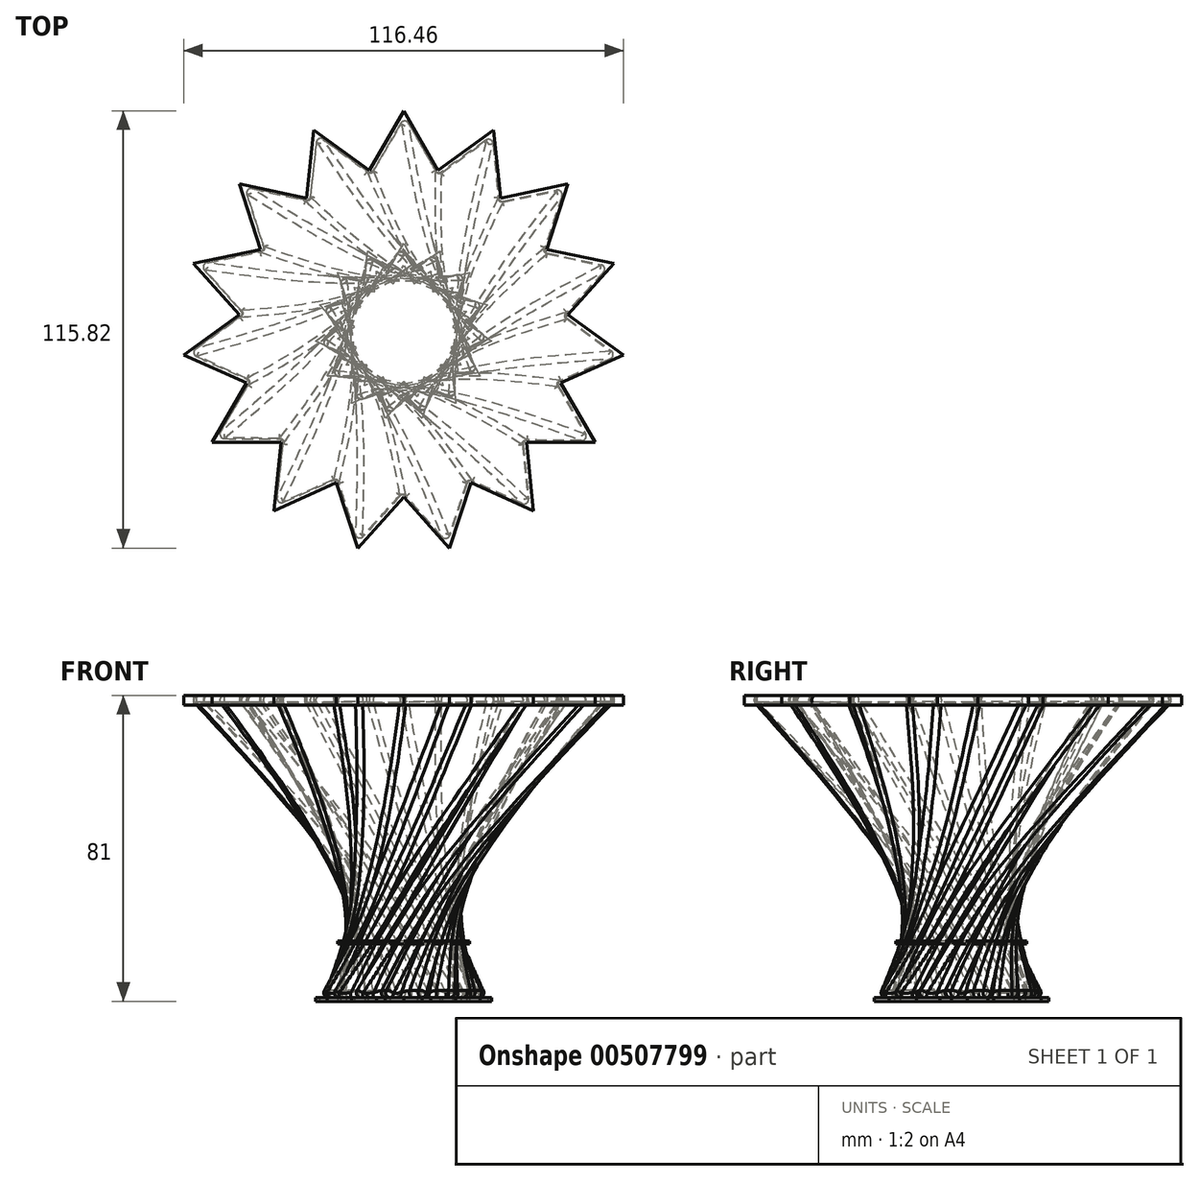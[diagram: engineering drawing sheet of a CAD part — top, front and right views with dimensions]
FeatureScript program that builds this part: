
annotation { "Feature Type Name" : "Feature", "Feature Type Description" : "" }
export const myFeature = defineFeature(function(context is Context, id is Id, definition is map)
    precondition{}
    {
        {
            assignVariable(context, id + "F0", {"name" : "BottomHeight", "anyValue" : 15});
        }
        {
            assignVariable(context, id + "F1", {"name" : "TopHeight", "anyValue" : 65});
        }
        {
            assignVariable(context, id + "F2", {"name" : "MiddleRatio", "anyValue" : 0.75});
        }
        {
            assignVariable(context, id + "F3", {"name" : "TopRatio", "anyValue" : 2.5});
        }
        {
            var Q0;
            Q0=qCreatedBy(makeId("Top.planeOp"),FACE);
            var sketch = newSketch(context, id + "F4", { "sketchPlane" : qUnion([Q0])});
            skCircle(sketch, "E0", {"center": v(0, 0) * mm, "radius": 17.5 * mm, "construction": true});
            skLineSegment(sketch, "E1", {"start": v(0, 0) * mm, "end": v(-3.64, 17.12) * mm, "construction": true});
            skLineSegment(sketch, "E2", {"start": v(-3.64, 17.12) * mm, "end": v(3.64, 17.12) * mm, "construction": true});
            skLineSegment(sketch, "E3", {"start": v(3.64, 17.12) * mm, "end": v(0, 0) * mm, "construction": true});
            skLineSegment(sketch, "E4", {"start": v(-3.64, 17.12) * mm, "end": v(0, 23.42) * mm});
            skLineSegment(sketch, "E5", {"start": v(0, 23.42) * mm, "end": v(3.64, 17.12) * mm});
            skLineSegment(sketch, "E6.1.0", {"start": v(-10.29, 14.16) * mm, "end": v(-9.53, 21.4) * mm});
            skLineSegment(sketch, "E6.1.1", {"start": v(-9.53, 21.4) * mm, "end": v(-3.64, 17.12) * mm});
            skLineSegment(sketch, "E6.2.0", {"start": v(-15.16, 8.75) * mm, "end": v(-17.4, 15.67) * mm});
            skLineSegment(sketch, "E6.2.1", {"start": v(-17.4, 15.67) * mm, "end": v(-10.29, 14.16) * mm});
            skLineSegment(sketch, "E6.3.0", {"start": v(-17.4, 1.83) * mm, "end": v(-22.27, 7.24) * mm});
            skLineSegment(sketch, "E6.3.1", {"start": v(-22.27, 7.24) * mm, "end": v(-15.16, 8.75) * mm});
            skLineSegment(sketch, "E6.4.0", {"start": v(-16.64, -5.4) * mm, "end": v(-23.3, -2.45) * mm});
            skLineSegment(sketch, "E6.4.1", {"start": v(-23.3, -2.45) * mm, "end": v(-17.4, 1.83) * mm});
            skLineSegment(sketch, "E6.5.0", {"start": v(-13, -11.7) * mm, "end": v(-20.28, -11.7) * mm});
            skLineSegment(sketch, "E6.5.1", {"start": v(-20.28, -11.7) * mm, "end": v(-16.64, -5.4) * mm});
            skLineSegment(sketch, "E6.6.0", {"start": v(-7.12, -15.99) * mm, "end": v(-13.77, -18.95) * mm});
            skLineSegment(sketch, "E6.6.1", {"start": v(-13.77, -18.95) * mm, "end": v(-13, -11.7) * mm});
            skLineSegment(sketch, "E6.7.0", {"start": v(0, -17.5) * mm, "end": v(-4.87, -22.9) * mm});
            skLineSegment(sketch, "E6.7.1", {"start": v(-4.87, -22.9) * mm, "end": v(-7.12, -15.99) * mm});
            skLineSegment(sketch, "E7.1.8.0", {"start": v(7.12, -15.99) * mm, "end": v(4.87, -22.9) * mm});
            skLineSegment(sketch, "E7.3.8.0", {"start": v(4.87, -22.9) * mm, "end": v(0, -17.5) * mm});
            skLineSegment(sketch, "E7.1.9.0", {"start": v(13, -11.7) * mm, "end": v(13.77, -18.95) * mm});
            skLineSegment(sketch, "E7.3.9.0", {"start": v(13.77, -18.95) * mm, "end": v(7.12, -15.99) * mm});
            skLineSegment(sketch, "E8.1.10.0", {"start": v(16.64, -5.4) * mm, "end": v(20.28, -11.7) * mm});
            skLineSegment(sketch, "E8.3.10.0", {"start": v(20.28, -11.7) * mm, "end": v(13, -11.7) * mm});
            skLineSegment(sketch, "E8.1.11.0", {"start": v(17.4, 1.83) * mm, "end": v(23.3, -2.45) * mm});
            skLineSegment(sketch, "E8.3.11.0", {"start": v(23.3, -2.45) * mm, "end": v(16.64, -5.4) * mm});
            skLineSegment(sketch, "E8.1.12.0", {"start": v(15.16, 8.75) * mm, "end": v(22.27, 7.24) * mm});
            skLineSegment(sketch, "E8.3.12.0", {"start": v(22.27, 7.24) * mm, "end": v(17.4, 1.83) * mm});
            skLineSegment(sketch, "E8.1.13.0", {"start": v(10.29, 14.16) * mm, "end": v(17.4, 15.67) * mm});
            skLineSegment(sketch, "E8.3.13.0", {"start": v(17.4, 15.67) * mm, "end": v(15.16, 8.75) * mm});
            skLineSegment(sketch, "E8.1.14.0", {"start": v(3.64, 17.12) * mm, "end": v(9.53, 21.4) * mm});
            skLineSegment(sketch, "E8.3.14.0", {"start": v(9.53, 21.4) * mm, "end": v(10.29, 14.16) * mm});
            skSolve(sketch);
        }
        {
            var Q0;
            Q0=makeQuery(id+"F4.imprint","IMPRINT",FACE,{"disambiguationData":[TD([[makeQuery(id+"F4.imprint","IMPRINT",EDGE,{"derivedFrom":sQuery(id+"F4.wireOp",EDGE,"E4")}),-1.0]])]});
            extrude(context, id + "F5", {"entities" : qUnion([Q0]), "depth" : 1 * mm, "offsetDistance" : 25 * mm});
        }
        {
            var Q0;
            Q0=makeQuery(id+"F5.opExtrude","SWEPT_BODY",BODY,{"disambiguationData":[OSD([sQuery(id+"F4.wireOp",EDGE,"E4"),sQuery(id+"F4.wireOp",EDGE,"E5"),sQuery(id+"F4.wireOp",EDGE,"E6.1.0"),sQuery(id+"F4.wireOp",EDGE,"E6.1.1"),sQuery(id+"F4.wireOp",EDGE,"E6.2.0"),sQuery(id+"F4.wireOp",EDGE,"E6.2.1"),sQuery(id+"F4.wireOp",EDGE,"E6.3.0"),sQuery(id+"F4.wireOp",EDGE,"E6.3.1"),sQuery(id+"F4.wireOp",EDGE,"E6.4.0"),sQuery(id+"F4.wireOp",EDGE,"E6.4.1"),sQuery(id+"F4.wireOp",EDGE,"E6.5.0"),sQuery(id+"F4.wireOp",EDGE,"E6.5.1"),sQuery(id+"F4.wireOp",EDGE,"E6.6.0"),sQuery(id+"F4.wireOp",EDGE,"E6.6.1"),sQuery(id+"F4.wireOp",EDGE,"E6.7.0"),sQuery(id+"F4.wireOp",EDGE,"E6.7.1"),sQuery(id+"F4.wireOp",EDGE,"E7.1.8.0"),sQuery(id+"F4.wireOp",EDGE,"E7.3.8.0"),sQuery(id+"F4.wireOp",EDGE,"E7.1.9.0"),sQuery(id+"F4.wireOp",EDGE,"E7.3.9.0"),sQuery(id+"F4.wireOp",EDGE,"E8.1.10.0"),sQuery(id+"F4.wireOp",EDGE,"E8.3.10.0"),sQuery(id+"F4.wireOp",EDGE,"E8.1.11.0"),sQuery(id+"F4.wireOp",EDGE,"E8.3.11.0"),sQuery(id+"F4.wireOp",EDGE,"E8.1.12.0"),sQuery(id+"F4.wireOp",EDGE,"E8.3.12.0"),sQuery(id+"F4.wireOp",EDGE,"E8.1.13.0"),sQuery(id+"F4.wireOp",EDGE,"E8.3.13.0"),sQuery(id+"F4.wireOp",EDGE,"E8.1.14.0"),sQuery(id+"F4.wireOp",EDGE,"E8.3.14.0"),sQuery(id+"F4.wireOp",EDGE,"E8.1.15.0"),sQuery(id+"F4.wireOp",EDGE,"E8.3.15.0"),sQuery(id+"F4.wireOp",EDGE,"E8.1.16.0"),sQuery(id+"F4.wireOp",EDGE,"E8.3.16.0"),sQuery(id+"F4.wireOp",EDGE,"E8.1.17.0"),sQuery(id+"F4.wireOp",EDGE,"E8.3.17.0"),sQuery(id+"F4.wireOp",EDGE,"E8.1.18.0"),sQuery(id+"F4.wireOp",EDGE,"E8.3.18.0"),sQuery(id+"F4.wireOp",EDGE,"E8.1.19.0"),sQuery(id+"F4.wireOp",EDGE,"E8.3.19.0"),sQuery(id+"F4.wireOp",EDGE,"E8.1.20.0"),sQuery(id+"F4.wireOp",EDGE,"E8.3.20.0"),sQuery(id+"F4.wireOp",EDGE,"E8.1.21.0"),sQuery(id+"F4.wireOp",EDGE,"E8.3.21.0"),sQuery(id+"F4.wireOp",EDGE,"E8.1.22.0"),sQuery(id+"F4.wireOp",EDGE,"E8.3.22.0"),sQuery(id+"F4.wireOp",EDGE,"E8.1.23.0"),sQuery(id+"F4.wireOp",EDGE,"E8.3.23.0"),sQuery(id+"F4.wireOp",EDGE,"E8.1.24.0"),sQuery(id+"F4.wireOp",EDGE,"E8.3.24.0")])]});
            transform(context, id + "F6", {"entities" : qUnion([Q0]), "transformType" : TransformType.TRANSLATION_3D, "dx" : 0 * mm, "dy" : 0 * mm, "dz" : (getVariable(context, 'BottomHeight')) * mm, "makeCopy" : true});
        }
        {
            var Q0;
            Q0=makeQuery(id+"F6.opPattern","COPY",BODY,{"derivedFrom":makeQuery(id+"F5.opExtrude","SWEPT_BODY",BODY,{"disambiguationData":[OSD([sQuery(id+"F4.wireOp",EDGE,"E4"),sQuery(id+"F4.wireOp",EDGE,"E5"),sQuery(id+"F4.wireOp",EDGE,"E6.1.0"),sQuery(id+"F4.wireOp",EDGE,"E6.1.1"),sQuery(id+"F4.wireOp",EDGE,"E6.2.0"),sQuery(id+"F4.wireOp",EDGE,"E6.2.1"),sQuery(id+"F4.wireOp",EDGE,"E6.3.0"),sQuery(id+"F4.wireOp",EDGE,"E6.3.1"),sQuery(id+"F4.wireOp",EDGE,"E6.4.0"),sQuery(id+"F4.wireOp",EDGE,"E6.4.1"),sQuery(id+"F4.wireOp",EDGE,"E6.5.0"),sQuery(id+"F4.wireOp",EDGE,"E6.5.1"),sQuery(id+"F4.wireOp",EDGE,"E6.6.0"),sQuery(id+"F4.wireOp",EDGE,"E6.6.1"),sQuery(id+"F4.wireOp",EDGE,"E6.7.0"),sQuery(id+"F4.wireOp",EDGE,"E6.7.1"),sQuery(id+"F4.wireOp",EDGE,"E7.1.8.0"),sQuery(id+"F4.wireOp",EDGE,"E7.3.8.0"),sQuery(id+"F4.wireOp",EDGE,"E7.1.9.0"),sQuery(id+"F4.wireOp",EDGE,"E7.3.9.0"),sQuery(id+"F4.wireOp",EDGE,"E8.1.10.0"),sQuery(id+"F4.wireOp",EDGE,"E8.3.10.0"),sQuery(id+"F4.wireOp",EDGE,"E8.1.11.0"),sQuery(id+"F4.wireOp",EDGE,"E8.3.11.0"),sQuery(id+"F4.wireOp",EDGE,"E8.1.12.0"),sQuery(id+"F4.wireOp",EDGE,"E8.3.12.0"),sQuery(id+"F4.wireOp",EDGE,"E8.1.13.0"),sQuery(id+"F4.wireOp",EDGE,"E8.3.13.0"),sQuery(id+"F4.wireOp",EDGE,"E8.1.14.0"),sQuery(id+"F4.wireOp",EDGE,"E8.3.14.0"),sQuery(id+"F4.wireOp",EDGE,"E8.1.15.0"),sQuery(id+"F4.wireOp",EDGE,"E8.3.15.0"),sQuery(id+"F4.wireOp",EDGE,"E8.1.16.0"),sQuery(id+"F4.wireOp",EDGE,"E8.3.16.0"),sQuery(id+"F4.wireOp",EDGE,"E8.1.17.0"),sQuery(id+"F4.wireOp",EDGE,"E8.3.17.0"),sQuery(id+"F4.wireOp",EDGE,"E8.1.18.0"),sQuery(id+"F4.wireOp",EDGE,"E8.3.18.0"),sQuery(id+"F4.wireOp",EDGE,"E8.1.19.0"),sQuery(id+"F4.wireOp",EDGE,"E8.3.19.0"),sQuery(id+"F4.wireOp",EDGE,"E8.1.20.0"),sQuery(id+"F4.wireOp",EDGE,"E8.3.20.0"),sQuery(id+"F4.wireOp",EDGE,"E8.1.21.0"),sQuery(id+"F4.wireOp",EDGE,"E8.3.21.0"),sQuery(id+"F4.wireOp",EDGE,"E8.1.22.0"),sQuery(id+"F4.wireOp",EDGE,"E8.3.22.0"),sQuery(id+"F4.wireOp",EDGE,"E8.1.23.0"),sQuery(id+"F4.wireOp",EDGE,"E8.3.23.0"),sQuery(id+"F4.wireOp",EDGE,"E8.1.24.0"),sQuery(id+"F4.wireOp",EDGE,"E8.3.24.0")])]}),"instanceName":"1"});
            transform(context, id + "F7", {"entities" : qUnion([Q0]), "transformType" : TransformType.TRANSLATION_3D, "dx" : 0 * mm, "dy" : 0 * mm, "dz" : (getVariable(context, 'TopHeight')) * mm, "makeCopy" : true});
        }
        {
            var Q0;
            Q0=makeQuery(id+"F6.opPattern","COPY",FACE,{"derivedFrom":makeQuery(id+"F5.opExtrude","CAP_FACE",FACE,{"disambiguationData":[OSD([sQuery(id+"F4.wireOp",EDGE,"E4"),sQuery(id+"F4.wireOp",EDGE,"E5"),sQuery(id+"F4.wireOp",EDGE,"E6.1.0"),sQuery(id+"F4.wireOp",EDGE,"E6.1.1"),sQuery(id+"F4.wireOp",EDGE,"E6.2.0"),sQuery(id+"F4.wireOp",EDGE,"E6.2.1"),sQuery(id+"F4.wireOp",EDGE,"E6.3.0"),sQuery(id+"F4.wireOp",EDGE,"E6.3.1"),sQuery(id+"F4.wireOp",EDGE,"E6.4.0"),sQuery(id+"F4.wireOp",EDGE,"E6.4.1"),sQuery(id+"F4.wireOp",EDGE,"E6.5.0"),sQuery(id+"F4.wireOp",EDGE,"E6.5.1"),sQuery(id+"F4.wireOp",EDGE,"E6.6.0"),sQuery(id+"F4.wireOp",EDGE,"E6.6.1"),sQuery(id+"F4.wireOp",EDGE,"E6.7.0"),sQuery(id+"F4.wireOp",EDGE,"E6.7.1"),sQuery(id+"F4.wireOp",EDGE,"E7.1.8.0"),sQuery(id+"F4.wireOp",EDGE,"E7.3.8.0"),sQuery(id+"F4.wireOp",EDGE,"E7.1.9.0"),sQuery(id+"F4.wireOp",EDGE,"E7.3.9.0"),sQuery(id+"F4.wireOp",EDGE,"E8.1.10.0"),sQuery(id+"F4.wireOp",EDGE,"E8.3.10.0"),sQuery(id+"F4.wireOp",EDGE,"E8.1.11.0"),sQuery(id+"F4.wireOp",EDGE,"E8.3.11.0"),sQuery(id+"F4.wireOp",EDGE,"E8.1.12.0"),sQuery(id+"F4.wireOp",EDGE,"E8.3.12.0"),sQuery(id+"F4.wireOp",EDGE,"E8.1.13.0"),sQuery(id+"F4.wireOp",EDGE,"E8.3.13.0"),sQuery(id+"F4.wireOp",EDGE,"E8.1.14.0"),sQuery(id+"F4.wireOp",EDGE,"E8.3.14.0"),sQuery(id+"F4.wireOp",EDGE,"E8.1.15.0"),sQuery(id+"F4.wireOp",EDGE,"E8.3.15.0"),sQuery(id+"F4.wireOp",EDGE,"E8.1.16.0"),sQuery(id+"F4.wireOp",EDGE,"E8.3.16.0"),sQuery(id+"F4.wireOp",EDGE,"E8.1.17.0"),sQuery(id+"F4.wireOp",EDGE,"E8.3.17.0"),sQuery(id+"F4.wireOp",EDGE,"E8.1.18.0"),sQuery(id+"F4.wireOp",EDGE,"E8.3.18.0"),sQuery(id+"F4.wireOp",EDGE,"E8.1.19.0"),sQuery(id+"F4.wireOp",EDGE,"E8.3.19.0"),sQuery(id+"F4.wireOp",EDGE,"E8.1.20.0"),sQuery(id+"F4.wireOp",EDGE,"E8.3.20.0"),sQuery(id+"F4.wireOp",EDGE,"E8.1.21.0"),sQuery(id+"F4.wireOp",EDGE,"E8.3.21.0"),sQuery(id+"F4.wireOp",EDGE,"E8.1.22.0"),sQuery(id+"F4.wireOp",EDGE,"E8.3.22.0"),sQuery(id+"F4.wireOp",EDGE,"E8.1.23.0"),sQuery(id+"F4.wireOp",EDGE,"E8.3.23.0"),sQuery(id+"F4.wireOp",EDGE,"E8.1.24.0"),sQuery(id+"F4.wireOp",EDGE,"E8.3.24.0")])],"isStart":false}),"instanceName":"1"});
            var sketch = newSketch(context, id + "F8", { "sketchPlane" : qUnion([Q0])});
            skPoint(sketch, "E9.0", {"position": v(0, 0) * mm});
            skSolve(sketch);
        }
        {
            var Q0;
            Q0=makeQuery(id+"F7.opPattern","COPY",FACE,{"derivedFrom":makeQuery(id+"F6.opPattern","COPY",FACE,{"derivedFrom":makeQuery(id+"F5.opExtrude","CAP_FACE",FACE,{"disambiguationData":[OSD([sQuery(id+"F4.wireOp",EDGE,"E4"),sQuery(id+"F4.wireOp",EDGE,"E5"),sQuery(id+"F4.wireOp",EDGE,"E6.1.0"),sQuery(id+"F4.wireOp",EDGE,"E6.1.1"),sQuery(id+"F4.wireOp",EDGE,"E6.2.0"),sQuery(id+"F4.wireOp",EDGE,"E6.2.1"),sQuery(id+"F4.wireOp",EDGE,"E6.3.0"),sQuery(id+"F4.wireOp",EDGE,"E6.3.1"),sQuery(id+"F4.wireOp",EDGE,"E6.4.0"),sQuery(id+"F4.wireOp",EDGE,"E6.4.1"),sQuery(id+"F4.wireOp",EDGE,"E6.5.0"),sQuery(id+"F4.wireOp",EDGE,"E6.5.1"),sQuery(id+"F4.wireOp",EDGE,"E6.6.0"),sQuery(id+"F4.wireOp",EDGE,"E6.6.1"),sQuery(id+"F4.wireOp",EDGE,"E6.7.0"),sQuery(id+"F4.wireOp",EDGE,"E6.7.1"),sQuery(id+"F4.wireOp",EDGE,"E7.1.8.0"),sQuery(id+"F4.wireOp",EDGE,"E7.3.8.0"),sQuery(id+"F4.wireOp",EDGE,"E7.1.9.0"),sQuery(id+"F4.wireOp",EDGE,"E7.3.9.0"),sQuery(id+"F4.wireOp",EDGE,"E8.1.10.0"),sQuery(id+"F4.wireOp",EDGE,"E8.3.10.0"),sQuery(id+"F4.wireOp",EDGE,"E8.1.11.0"),sQuery(id+"F4.wireOp",EDGE,"E8.3.11.0"),sQuery(id+"F4.wireOp",EDGE,"E8.1.12.0"),sQuery(id+"F4.wireOp",EDGE,"E8.3.12.0"),sQuery(id+"F4.wireOp",EDGE,"E8.1.13.0"),sQuery(id+"F4.wireOp",EDGE,"E8.3.13.0"),sQuery(id+"F4.wireOp",EDGE,"E8.1.14.0"),sQuery(id+"F4.wireOp",EDGE,"E8.3.14.0"),sQuery(id+"F4.wireOp",EDGE,"E8.1.15.0"),sQuery(id+"F4.wireOp",EDGE,"E8.3.15.0"),sQuery(id+"F4.wireOp",EDGE,"E8.1.16.0"),sQuery(id+"F4.wireOp",EDGE,"E8.3.16.0"),sQuery(id+"F4.wireOp",EDGE,"E8.1.17.0"),sQuery(id+"F4.wireOp",EDGE,"E8.3.17.0"),sQuery(id+"F4.wireOp",EDGE,"E8.1.18.0"),sQuery(id+"F4.wireOp",EDGE,"E8.3.18.0"),sQuery(id+"F4.wireOp",EDGE,"E8.1.19.0"),sQuery(id+"F4.wireOp",EDGE,"E8.3.19.0"),sQuery(id+"F4.wireOp",EDGE,"E8.1.20.0"),sQuery(id+"F4.wireOp",EDGE,"E8.3.20.0"),sQuery(id+"F4.wireOp",EDGE,"E8.1.21.0"),sQuery(id+"F4.wireOp",EDGE,"E8.3.21.0"),sQuery(id+"F4.wireOp",EDGE,"E8.1.22.0"),sQuery(id+"F4.wireOp",EDGE,"E8.3.22.0"),sQuery(id+"F4.wireOp",EDGE,"E8.1.23.0"),sQuery(id+"F4.wireOp",EDGE,"E8.3.23.0"),sQuery(id+"F4.wireOp",EDGE,"E8.1.24.0"),sQuery(id+"F4.wireOp",EDGE,"E8.3.24.0")])],"isStart":false}),"instanceName":"1"}),"instanceName":"1"});
            var sketch = newSketch(context, id + "F9", { "sketchPlane" : qUnion([Q0])});
            skPoint(sketch, "E10.0", {"position": v(0, 0) * mm});
            skSolve(sketch);
        }
        {
            var Q0;
            Q0=makeQuery(id+"F6.opPattern","COPY",BODY,{"derivedFrom":makeQuery(id+"F5.opExtrude","SWEPT_BODY",BODY,{"disambiguationData":[OSD([sQuery(id+"F4.wireOp",EDGE,"E4"),sQuery(id+"F4.wireOp",EDGE,"E5"),sQuery(id+"F4.wireOp",EDGE,"E6.1.0"),sQuery(id+"F4.wireOp",EDGE,"E6.1.1"),sQuery(id+"F4.wireOp",EDGE,"E6.2.0"),sQuery(id+"F4.wireOp",EDGE,"E6.2.1"),sQuery(id+"F4.wireOp",EDGE,"E6.3.0"),sQuery(id+"F4.wireOp",EDGE,"E6.3.1"),sQuery(id+"F4.wireOp",EDGE,"E6.4.0"),sQuery(id+"F4.wireOp",EDGE,"E6.4.1"),sQuery(id+"F4.wireOp",EDGE,"E6.5.0"),sQuery(id+"F4.wireOp",EDGE,"E6.5.1"),sQuery(id+"F4.wireOp",EDGE,"E6.6.0"),sQuery(id+"F4.wireOp",EDGE,"E6.6.1"),sQuery(id+"F4.wireOp",EDGE,"E6.7.0"),sQuery(id+"F4.wireOp",EDGE,"E6.7.1"),sQuery(id+"F4.wireOp",EDGE,"E7.1.8.0"),sQuery(id+"F4.wireOp",EDGE,"E7.3.8.0"),sQuery(id+"F4.wireOp",EDGE,"E7.1.9.0"),sQuery(id+"F4.wireOp",EDGE,"E7.3.9.0"),sQuery(id+"F4.wireOp",EDGE,"E8.1.10.0"),sQuery(id+"F4.wireOp",EDGE,"E8.3.10.0"),sQuery(id+"F4.wireOp",EDGE,"E8.1.11.0"),sQuery(id+"F4.wireOp",EDGE,"E8.3.11.0"),sQuery(id+"F4.wireOp",EDGE,"E8.1.12.0"),sQuery(id+"F4.wireOp",EDGE,"E8.3.12.0"),sQuery(id+"F4.wireOp",EDGE,"E8.1.13.0"),sQuery(id+"F4.wireOp",EDGE,"E8.3.13.0"),sQuery(id+"F4.wireOp",EDGE,"E8.1.14.0"),sQuery(id+"F4.wireOp",EDGE,"E8.3.14.0"),sQuery(id+"F4.wireOp",EDGE,"E8.1.15.0"),sQuery(id+"F4.wireOp",EDGE,"E8.3.15.0"),sQuery(id+"F4.wireOp",EDGE,"E8.1.16.0"),sQuery(id+"F4.wireOp",EDGE,"E8.3.16.0"),sQuery(id+"F4.wireOp",EDGE,"E8.1.17.0"),sQuery(id+"F4.wireOp",EDGE,"E8.3.17.0"),sQuery(id+"F4.wireOp",EDGE,"E8.1.18.0"),sQuery(id+"F4.wireOp",EDGE,"E8.3.18.0"),sQuery(id+"F4.wireOp",EDGE,"E8.1.19.0"),sQuery(id+"F4.wireOp",EDGE,"E8.3.19.0"),sQuery(id+"F4.wireOp",EDGE,"E8.1.20.0"),sQuery(id+"F4.wireOp",EDGE,"E8.3.20.0"),sQuery(id+"F4.wireOp",EDGE,"E8.1.21.0"),sQuery(id+"F4.wireOp",EDGE,"E8.3.21.0"),sQuery(id+"F4.wireOp",EDGE,"E8.1.22.0"),sQuery(id+"F4.wireOp",EDGE,"E8.3.22.0"),sQuery(id+"F4.wireOp",EDGE,"E8.1.23.0"),sQuery(id+"F4.wireOp",EDGE,"E8.3.23.0"),sQuery(id+"F4.wireOp",EDGE,"E8.1.24.0"),sQuery(id+"F4.wireOp",EDGE,"E8.3.24.0")])]}),"instanceName":"1"});
            var Q1;
            Q1=sQuery(id+"F8.wireOp",VERTEX,"E9.0");
            transform(context, id + "F10", {"entities" : qUnion([Q0]), "transformType" : TransformType.SCALE_UNIFORMLY, "scale" : getVariable(context, 'MiddleRatio'), "scalePoint" : qUnion([Q1]), "makeCopy" : false});
        }
        {
            var Q0;
            Q0=makeQuery(id+"F7.opPattern","COPY",BODY,{"derivedFrom":makeQuery(id+"F6.opPattern","COPY",BODY,{"derivedFrom":makeQuery(id+"F5.opExtrude","SWEPT_BODY",BODY,{"disambiguationData":[OSD([sQuery(id+"F4.wireOp",EDGE,"E4"),sQuery(id+"F4.wireOp",EDGE,"E5"),sQuery(id+"F4.wireOp",EDGE,"E6.1.0"),sQuery(id+"F4.wireOp",EDGE,"E6.1.1"),sQuery(id+"F4.wireOp",EDGE,"E6.2.0"),sQuery(id+"F4.wireOp",EDGE,"E6.2.1"),sQuery(id+"F4.wireOp",EDGE,"E6.3.0"),sQuery(id+"F4.wireOp",EDGE,"E6.3.1"),sQuery(id+"F4.wireOp",EDGE,"E6.4.0"),sQuery(id+"F4.wireOp",EDGE,"E6.4.1"),sQuery(id+"F4.wireOp",EDGE,"E6.5.0"),sQuery(id+"F4.wireOp",EDGE,"E6.5.1"),sQuery(id+"F4.wireOp",EDGE,"E6.6.0"),sQuery(id+"F4.wireOp",EDGE,"E6.6.1"),sQuery(id+"F4.wireOp",EDGE,"E6.7.0"),sQuery(id+"F4.wireOp",EDGE,"E6.7.1"),sQuery(id+"F4.wireOp",EDGE,"E7.1.8.0"),sQuery(id+"F4.wireOp",EDGE,"E7.3.8.0"),sQuery(id+"F4.wireOp",EDGE,"E7.1.9.0"),sQuery(id+"F4.wireOp",EDGE,"E7.3.9.0"),sQuery(id+"F4.wireOp",EDGE,"E8.1.10.0"),sQuery(id+"F4.wireOp",EDGE,"E8.3.10.0"),sQuery(id+"F4.wireOp",EDGE,"E8.1.11.0"),sQuery(id+"F4.wireOp",EDGE,"E8.3.11.0"),sQuery(id+"F4.wireOp",EDGE,"E8.1.12.0"),sQuery(id+"F4.wireOp",EDGE,"E8.3.12.0"),sQuery(id+"F4.wireOp",EDGE,"E8.1.13.0"),sQuery(id+"F4.wireOp",EDGE,"E8.3.13.0"),sQuery(id+"F4.wireOp",EDGE,"E8.1.14.0"),sQuery(id+"F4.wireOp",EDGE,"E8.3.14.0"),sQuery(id+"F4.wireOp",EDGE,"E8.1.15.0"),sQuery(id+"F4.wireOp",EDGE,"E8.3.15.0"),sQuery(id+"F4.wireOp",EDGE,"E8.1.16.0"),sQuery(id+"F4.wireOp",EDGE,"E8.3.16.0"),sQuery(id+"F4.wireOp",EDGE,"E8.1.17.0"),sQuery(id+"F4.wireOp",EDGE,"E8.3.17.0"),sQuery(id+"F4.wireOp",EDGE,"E8.1.18.0"),sQuery(id+"F4.wireOp",EDGE,"E8.3.18.0"),sQuery(id+"F4.wireOp",EDGE,"E8.1.19.0"),sQuery(id+"F4.wireOp",EDGE,"E8.3.19.0"),sQuery(id+"F4.wireOp",EDGE,"E8.1.20.0"),sQuery(id+"F4.wireOp",EDGE,"E8.3.20.0"),sQuery(id+"F4.wireOp",EDGE,"E8.1.21.0"),sQuery(id+"F4.wireOp",EDGE,"E8.3.21.0"),sQuery(id+"F4.wireOp",EDGE,"E8.1.22.0"),sQuery(id+"F4.wireOp",EDGE,"E8.3.22.0"),sQuery(id+"F4.wireOp",EDGE,"E8.1.23.0"),sQuery(id+"F4.wireOp",EDGE,"E8.3.23.0"),sQuery(id+"F4.wireOp",EDGE,"E8.1.24.0"),sQuery(id+"F4.wireOp",EDGE,"E8.3.24.0")])]}),"instanceName":"1"}),"instanceName":"1"});
            var Q1;
            Q1=sQuery(id+"F9.wireOp",VERTEX,"E10.0");
            transform(context, id + "F11", {"entities" : qUnion([Q0]), "transformType" : TransformType.SCALE_UNIFORMLY, "scale" : getVariable(context, 'TopRatio'), "scalePoint" : qUnion([Q1]), "makeCopy" : false});
        }
        {
            var Q0;
            Q0=makeQuery(id+"F5.opExtrude","CAP_FACE",FACE,{"disambiguationData":[OSD([sQuery(id+"F4.wireOp",EDGE,"E4"),sQuery(id+"F4.wireOp",EDGE,"E5"),sQuery(id+"F4.wireOp",EDGE,"E6.1.0"),sQuery(id+"F4.wireOp",EDGE,"E6.1.1"),sQuery(id+"F4.wireOp",EDGE,"E6.2.0"),sQuery(id+"F4.wireOp",EDGE,"E6.2.1"),sQuery(id+"F4.wireOp",EDGE,"E6.3.0"),sQuery(id+"F4.wireOp",EDGE,"E6.3.1"),sQuery(id+"F4.wireOp",EDGE,"E6.4.0"),sQuery(id+"F4.wireOp",EDGE,"E6.4.1"),sQuery(id+"F4.wireOp",EDGE,"E6.5.0"),sQuery(id+"F4.wireOp",EDGE,"E6.5.1"),sQuery(id+"F4.wireOp",EDGE,"E6.6.0"),sQuery(id+"F4.wireOp",EDGE,"E6.6.1"),sQuery(id+"F4.wireOp",EDGE,"E6.7.0"),sQuery(id+"F4.wireOp",EDGE,"E6.7.1"),sQuery(id+"F4.wireOp",EDGE,"E7.1.8.0"),sQuery(id+"F4.wireOp",EDGE,"E7.3.8.0"),sQuery(id+"F4.wireOp",EDGE,"E7.1.9.0"),sQuery(id+"F4.wireOp",EDGE,"E7.3.9.0"),sQuery(id+"F4.wireOp",EDGE,"E8.1.10.0"),sQuery(id+"F4.wireOp",EDGE,"E8.3.10.0"),sQuery(id+"F4.wireOp",EDGE,"E8.1.11.0"),sQuery(id+"F4.wireOp",EDGE,"E8.3.11.0"),sQuery(id+"F4.wireOp",EDGE,"E8.1.12.0"),sQuery(id+"F4.wireOp",EDGE,"E8.3.12.0"),sQuery(id+"F4.wireOp",EDGE,"E8.1.13.0"),sQuery(id+"F4.wireOp",EDGE,"E8.3.13.0"),sQuery(id+"F4.wireOp",EDGE,"E8.1.14.0"),sQuery(id+"F4.wireOp",EDGE,"E8.3.14.0"),sQuery(id+"F4.wireOp",EDGE,"E8.1.15.0"),sQuery(id+"F4.wireOp",EDGE,"E8.3.15.0"),sQuery(id+"F4.wireOp",EDGE,"E8.1.16.0"),sQuery(id+"F4.wireOp",EDGE,"E8.3.16.0"),sQuery(id+"F4.wireOp",EDGE,"E8.1.17.0"),sQuery(id+"F4.wireOp",EDGE,"E8.3.17.0"),sQuery(id+"F4.wireOp",EDGE,"E8.1.18.0"),sQuery(id+"F4.wireOp",EDGE,"E8.3.18.0"),sQuery(id+"F4.wireOp",EDGE,"E8.1.19.0"),sQuery(id+"F4.wireOp",EDGE,"E8.3.19.0"),sQuery(id+"F4.wireOp",EDGE,"E8.1.20.0"),sQuery(id+"F4.wireOp",EDGE,"E8.3.20.0"),sQuery(id+"F4.wireOp",EDGE,"E8.1.21.0"),sQuery(id+"F4.wireOp",EDGE,"E8.3.21.0"),sQuery(id+"F4.wireOp",EDGE,"E8.1.22.0"),sQuery(id+"F4.wireOp",EDGE,"E8.3.22.0"),sQuery(id+"F4.wireOp",EDGE,"E8.1.23.0"),sQuery(id+"F4.wireOp",EDGE,"E8.3.23.0"),sQuery(id+"F4.wireOp",EDGE,"E8.1.24.0"),sQuery(id+"F4.wireOp",EDGE,"E8.3.24.0")])],"isStart":false});
            var Q1;
            Q1=makeQuery(id+"F6.opPattern","COPY",FACE,{"derivedFrom":makeQuery(id+"F5.opExtrude","CAP_FACE",FACE,{"disambiguationData":[OSD([sQuery(id+"F4.wireOp",EDGE,"E4"),sQuery(id+"F4.wireOp",EDGE,"E5"),sQuery(id+"F4.wireOp",EDGE,"E6.1.0"),sQuery(id+"F4.wireOp",EDGE,"E6.1.1"),sQuery(id+"F4.wireOp",EDGE,"E6.2.0"),sQuery(id+"F4.wireOp",EDGE,"E6.2.1"),sQuery(id+"F4.wireOp",EDGE,"E6.3.0"),sQuery(id+"F4.wireOp",EDGE,"E6.3.1"),sQuery(id+"F4.wireOp",EDGE,"E6.4.0"),sQuery(id+"F4.wireOp",EDGE,"E6.4.1"),sQuery(id+"F4.wireOp",EDGE,"E6.5.0"),sQuery(id+"F4.wireOp",EDGE,"E6.5.1"),sQuery(id+"F4.wireOp",EDGE,"E6.6.0"),sQuery(id+"F4.wireOp",EDGE,"E6.6.1"),sQuery(id+"F4.wireOp",EDGE,"E6.7.0"),sQuery(id+"F4.wireOp",EDGE,"E6.7.1"),sQuery(id+"F4.wireOp",EDGE,"E7.1.8.0"),sQuery(id+"F4.wireOp",EDGE,"E7.3.8.0"),sQuery(id+"F4.wireOp",EDGE,"E7.1.9.0"),sQuery(id+"F4.wireOp",EDGE,"E7.3.9.0"),sQuery(id+"F4.wireOp",EDGE,"E8.1.10.0"),sQuery(id+"F4.wireOp",EDGE,"E8.3.10.0"),sQuery(id+"F4.wireOp",EDGE,"E8.1.11.0"),sQuery(id+"F4.wireOp",EDGE,"E8.3.11.0"),sQuery(id+"F4.wireOp",EDGE,"E8.1.12.0"),sQuery(id+"F4.wireOp",EDGE,"E8.3.12.0"),sQuery(id+"F4.wireOp",EDGE,"E8.1.13.0"),sQuery(id+"F4.wireOp",EDGE,"E8.3.13.0"),sQuery(id+"F4.wireOp",EDGE,"E8.1.14.0"),sQuery(id+"F4.wireOp",EDGE,"E8.3.14.0"),sQuery(id+"F4.wireOp",EDGE,"E8.1.15.0"),sQuery(id+"F4.wireOp",EDGE,"E8.3.15.0"),sQuery(id+"F4.wireOp",EDGE,"E8.1.16.0"),sQuery(id+"F4.wireOp",EDGE,"E8.3.16.0"),sQuery(id+"F4.wireOp",EDGE,"E8.1.17.0"),sQuery(id+"F4.wireOp",EDGE,"E8.3.17.0"),sQuery(id+"F4.wireOp",EDGE,"E8.1.18.0"),sQuery(id+"F4.wireOp",EDGE,"E8.3.18.0"),sQuery(id+"F4.wireOp",EDGE,"E8.1.19.0"),sQuery(id+"F4.wireOp",EDGE,"E8.3.19.0"),sQuery(id+"F4.wireOp",EDGE,"E8.1.20.0"),sQuery(id+"F4.wireOp",EDGE,"E8.3.20.0"),sQuery(id+"F4.wireOp",EDGE,"E8.1.21.0"),sQuery(id+"F4.wireOp",EDGE,"E8.3.21.0"),sQuery(id+"F4.wireOp",EDGE,"E8.1.22.0"),sQuery(id+"F4.wireOp",EDGE,"E8.3.22.0"),sQuery(id+"F4.wireOp",EDGE,"E8.1.23.0"),sQuery(id+"F4.wireOp",EDGE,"E8.3.23.0"),sQuery(id+"F4.wireOp",EDGE,"E8.1.24.0"),sQuery(id+"F4.wireOp",EDGE,"E8.3.24.0")])],"isStart":false}),"instanceName":"1"});
            var Q2;
            Q2=makeQuery(id+"F7.opPattern","COPY",FACE,{"derivedFrom":makeQuery(id+"F6.opPattern","COPY",FACE,{"derivedFrom":makeQuery(id+"F5.opExtrude","CAP_FACE",FACE,{"disambiguationData":[OSD([sQuery(id+"F4.wireOp",EDGE,"E4"),sQuery(id+"F4.wireOp",EDGE,"E5"),sQuery(id+"F4.wireOp",EDGE,"E6.1.0"),sQuery(id+"F4.wireOp",EDGE,"E6.1.1"),sQuery(id+"F4.wireOp",EDGE,"E6.2.0"),sQuery(id+"F4.wireOp",EDGE,"E6.2.1"),sQuery(id+"F4.wireOp",EDGE,"E6.3.0"),sQuery(id+"F4.wireOp",EDGE,"E6.3.1"),sQuery(id+"F4.wireOp",EDGE,"E6.4.0"),sQuery(id+"F4.wireOp",EDGE,"E6.4.1"),sQuery(id+"F4.wireOp",EDGE,"E6.5.0"),sQuery(id+"F4.wireOp",EDGE,"E6.5.1"),sQuery(id+"F4.wireOp",EDGE,"E6.6.0"),sQuery(id+"F4.wireOp",EDGE,"E6.6.1"),sQuery(id+"F4.wireOp",EDGE,"E6.7.0"),sQuery(id+"F4.wireOp",EDGE,"E6.7.1"),sQuery(id+"F4.wireOp",EDGE,"E7.1.8.0"),sQuery(id+"F4.wireOp",EDGE,"E7.3.8.0"),sQuery(id+"F4.wireOp",EDGE,"E7.1.9.0"),sQuery(id+"F4.wireOp",EDGE,"E7.3.9.0"),sQuery(id+"F4.wireOp",EDGE,"E8.1.10.0"),sQuery(id+"F4.wireOp",EDGE,"E8.3.10.0"),sQuery(id+"F4.wireOp",EDGE,"E8.1.11.0"),sQuery(id+"F4.wireOp",EDGE,"E8.3.11.0"),sQuery(id+"F4.wireOp",EDGE,"E8.1.12.0"),sQuery(id+"F4.wireOp",EDGE,"E8.3.12.0"),sQuery(id+"F4.wireOp",EDGE,"E8.1.13.0"),sQuery(id+"F4.wireOp",EDGE,"E8.3.13.0"),sQuery(id+"F4.wireOp",EDGE,"E8.1.14.0"),sQuery(id+"F4.wireOp",EDGE,"E8.3.14.0"),sQuery(id+"F4.wireOp",EDGE,"E8.1.15.0"),sQuery(id+"F4.wireOp",EDGE,"E8.3.15.0"),sQuery(id+"F4.wireOp",EDGE,"E8.1.16.0"),sQuery(id+"F4.wireOp",EDGE,"E8.3.16.0"),sQuery(id+"F4.wireOp",EDGE,"E8.1.17.0"),sQuery(id+"F4.wireOp",EDGE,"E8.3.17.0"),sQuery(id+"F4.wireOp",EDGE,"E8.1.18.0"),sQuery(id+"F4.wireOp",EDGE,"E8.3.18.0"),sQuery(id+"F4.wireOp",EDGE,"E8.1.19.0"),sQuery(id+"F4.wireOp",EDGE,"E8.3.19.0"),sQuery(id+"F4.wireOp",EDGE,"E8.1.20.0"),sQuery(id+"F4.wireOp",EDGE,"E8.3.20.0"),sQuery(id+"F4.wireOp",EDGE,"E8.1.21.0"),sQuery(id+"F4.wireOp",EDGE,"E8.3.21.0"),sQuery(id+"F4.wireOp",EDGE,"E8.1.22.0"),sQuery(id+"F4.wireOp",EDGE,"E8.3.22.0"),sQuery(id+"F4.wireOp",EDGE,"E8.1.23.0"),sQuery(id+"F4.wireOp",EDGE,"E8.3.23.0"),sQuery(id+"F4.wireOp",EDGE,"E8.1.24.0"),sQuery(id+"F4.wireOp",EDGE,"E8.3.24.0")])],"isStart":false}),"instanceName":"1"}),"instanceName":"1"});
            var Q3;
            Q3=makeQuery(id+"F5.opExtrude","CAP_VERTEX",VERTEX,{"disambiguationData":[OSD([sQuery(id+"F4.wireOp",EDGE,"E6.1.0"),sQuery(id+"F4.wireOp",EDGE,"E6.1.1")])],"isStart":false});
            var Q4;
            Q4=makeQuery(id+"F6.opPattern","COPY",VERTEX,{"derivedFrom":makeQuery(id+"F5.opExtrude","CAP_VERTEX",VERTEX,{"disambiguationData":[OSD([sQuery(id+"F4.wireOp",EDGE,"E6.2.0"),sQuery(id+"F4.wireOp",EDGE,"E6.2.1")])],"isStart":false}),"instanceName":"1"});
            var Q5;
            Q5=makeQuery(id+"F7.opPattern","COPY",VERTEX,{"derivedFrom":makeQuery(id+"F6.opPattern","COPY",VERTEX,{"derivedFrom":makeQuery(id+"F5.opExtrude","CAP_VERTEX",VERTEX,{"disambiguationData":[OSD([sQuery(id+"F4.wireOp",EDGE,"E6.5.0"),sQuery(id+"F4.wireOp",EDGE,"E6.5.1")])],"isStart":false}),"instanceName":"1"}),"instanceName":"1"});
            loft(context, id + "F12", {"sheetProfilesArray" : [{ "sheetProfileEntities" : qUnion([Q0]) }, { "sheetProfileEntities" : qUnion([Q1]) }, { "sheetProfileEntities" : qUnion([Q2]) }], "matchConnections" : true, "connections" : [{ "connectionEntities" : qUnion([Q3, Q4, Q5]), "connectionEdgeQueries" : qUnion([]), "connectionEdgeParameters" : [] }]});
        }
        {
            var Q0;
            {var subQ0=sQuery(id+"F4.wireOp",EDGE,"E8.3.14.0");var subQ1=sQuery(id+"F4.wireOp",EDGE,"E8.1.14.0");var subQ2=sQuery(id+"F4.wireOp",EDGE,"E8.3.13.0");var subQ3=sQuery(id+"F4.wireOp",EDGE,"E8.1.13.0");var subQ4=sQuery(id+"F4.wireOp",EDGE,"E8.3.12.0");var subQ5=sQuery(id+"F4.wireOp",EDGE,"E8.1.12.0");var subQ6=sQuery(id+"F4.wireOp",EDGE,"E8.3.11.0");var subQ7=sQuery(id+"F4.wireOp",EDGE,"E8.1.11.0");var subQ8=sQuery(id+"F4.wireOp",EDGE,"E8.3.10.0");var subQ9=sQuery(id+"F4.wireOp",EDGE,"E8.1.10.0");var subQ10=sQuery(id+"F4.wireOp",EDGE,"E7.3.9.0");var subQ11=sQuery(id+"F4.wireOp",EDGE,"E7.1.9.0");var subQ12=sQuery(id+"F4.wireOp",EDGE,"E7.3.8.0");var subQ13=sQuery(id+"F4.wireOp",EDGE,"E7.1.8.0");var subQ14=sQuery(id+"F4.wireOp",EDGE,"E6.7.1");var subQ15=sQuery(id+"F4.wireOp",EDGE,"E6.7.0");var subQ16=sQuery(id+"F4.wireOp",EDGE,"E6.6.1");var subQ17=sQuery(id+"F4.wireOp",EDGE,"E6.6.0");var subQ18=sQuery(id+"F4.wireOp",EDGE,"E6.5.1");var subQ19=sQuery(id+"F4.wireOp",EDGE,"E6.5.0");var subQ20=sQuery(id+"F4.wireOp",EDGE,"E6.4.1");var subQ21=sQuery(id+"F4.wireOp",EDGE,"E6.4.0");var subQ22=sQuery(id+"F4.wireOp",EDGE,"E6.3.1");var subQ23=sQuery(id+"F4.wireOp",EDGE,"E6.3.0");var subQ24=sQuery(id+"F4.wireOp",EDGE,"E6.2.1");var subQ25=sQuery(id+"F4.wireOp",EDGE,"E6.2.0");var subQ26=sQuery(id+"F4.wireOp",EDGE,"E6.1.1");var subQ27=sQuery(id+"F4.wireOp",EDGE,"E6.1.0");var subQ28=sQuery(id+"F4.wireOp",EDGE,"E5");var subQ29=sQuery(id+"F4.wireOp",EDGE,"E4");Q0=makeQuery(id+"F12.opLoft","CAP_FACE",FACE,{"disambiguationData":[OSD([subQ29,subQ28,subQ27,subQ26,subQ25,subQ24,subQ23,subQ22,subQ21,subQ20,subQ19,subQ18,subQ17,subQ16,subQ15,subQ14,subQ13,subQ12,subQ11,subQ10,subQ9,subQ8,subQ7,subQ6,subQ5,subQ4,subQ3,subQ2,subQ1,subQ0]),TDD([makeQuery(id+"F7.opPattern","COPY",FACE,{"derivedFrom":makeQuery(id+"F6.opPattern","COPY",FACE,{"derivedFrom":makeQuery(id+"F5.opExtrude","CAP_FACE",FACE,{"disambiguationData":[OSD([subQ29,subQ28,subQ27,subQ26,subQ25,subQ24,subQ23,subQ22,subQ21,subQ20,subQ19,subQ18,subQ17,subQ16,subQ15,subQ14,subQ13,subQ12,subQ11,subQ10,subQ9,subQ8,subQ7,subQ6,subQ5,subQ4,subQ3,subQ2,subQ1,subQ0])],"isStart":false}),"instanceName":"1"}),"instanceName":"1"})])],"isStart":true});}
            var Q1;
            {var subQ0=sQuery(id+"F4.wireOp",EDGE,"E8.3.14.0");var subQ1=sQuery(id+"F4.wireOp",EDGE,"E8.1.14.0");var subQ2=sQuery(id+"F4.wireOp",EDGE,"E8.3.13.0");var subQ3=sQuery(id+"F4.wireOp",EDGE,"E8.1.13.0");var subQ4=sQuery(id+"F4.wireOp",EDGE,"E8.3.12.0");var subQ5=sQuery(id+"F4.wireOp",EDGE,"E8.1.12.0");var subQ6=sQuery(id+"F4.wireOp",EDGE,"E8.3.11.0");var subQ7=sQuery(id+"F4.wireOp",EDGE,"E8.1.11.0");var subQ8=sQuery(id+"F4.wireOp",EDGE,"E8.3.10.0");var subQ9=sQuery(id+"F4.wireOp",EDGE,"E8.1.10.0");var subQ10=sQuery(id+"F4.wireOp",EDGE,"E7.3.9.0");var subQ11=sQuery(id+"F4.wireOp",EDGE,"E7.1.9.0");var subQ12=sQuery(id+"F4.wireOp",EDGE,"E7.3.8.0");var subQ13=sQuery(id+"F4.wireOp",EDGE,"E7.1.8.0");var subQ14=sQuery(id+"F4.wireOp",EDGE,"E6.7.1");var subQ15=sQuery(id+"F4.wireOp",EDGE,"E6.7.0");var subQ16=sQuery(id+"F4.wireOp",EDGE,"E6.6.1");var subQ17=sQuery(id+"F4.wireOp",EDGE,"E6.6.0");var subQ18=sQuery(id+"F4.wireOp",EDGE,"E6.5.1");var subQ19=sQuery(id+"F4.wireOp",EDGE,"E6.5.0");var subQ20=sQuery(id+"F4.wireOp",EDGE,"E6.4.1");var subQ21=sQuery(id+"F4.wireOp",EDGE,"E6.4.0");var subQ22=sQuery(id+"F4.wireOp",EDGE,"E6.3.1");var subQ23=sQuery(id+"F4.wireOp",EDGE,"E6.3.0");var subQ24=sQuery(id+"F4.wireOp",EDGE,"E6.2.1");var subQ25=sQuery(id+"F4.wireOp",EDGE,"E6.2.0");var subQ26=sQuery(id+"F4.wireOp",EDGE,"E6.1.1");var subQ27=sQuery(id+"F4.wireOp",EDGE,"E6.1.0");var subQ28=sQuery(id+"F4.wireOp",EDGE,"E5");var subQ29=sQuery(id+"F4.wireOp",EDGE,"E4");Q1=makeQuery(id+"F12.opLoft","CAP_FACE",FACE,{"disambiguationData":[OSD([subQ29,subQ28,subQ27,subQ26,subQ25,subQ24,subQ23,subQ22,subQ21,subQ20,subQ19,subQ18,subQ17,subQ16,subQ15,subQ14,subQ13,subQ12,subQ11,subQ10,subQ9,subQ8,subQ7,subQ6,subQ5,subQ4,subQ3,subQ2,subQ1,subQ0]),TDD([makeQuery(id+"F5.opExtrude","CAP_FACE",FACE,{"disambiguationData":[OSD([subQ29,subQ28,subQ27,subQ26,subQ25,subQ24,subQ23,subQ22,subQ21,subQ20,subQ19,subQ18,subQ17,subQ16,subQ15,subQ14,subQ13,subQ12,subQ11,subQ10,subQ9,subQ8,subQ7,subQ6,subQ5,subQ4,subQ3,subQ2,subQ1,subQ0])],"isStart":false})])],"isStart":true});}
            var Q2;
            Q2=makeQuery(id+"F12.opLoft","SWEPT_EDGE",EDGE,{"disambiguationData":[OSD([sQuery(id+"F4.wireOp",EDGE,"E7.1.8.0"),sQuery(id+"F4.wireOp",EDGE,"E7.1.9.0"),sQuery(id+"F4.wireOp",EDGE,"E7.3.9.0"),sQuery(id+"F4.wireOp",EDGE,"E8.3.10.0")])]});
            var Q3;
            Q3=makeQuery(id+"F12.opLoft","MID_CAP_EDGE",EDGE,{"disambiguationData":[OSD([sQuery(id+"F4.wireOp",EDGE,"E7.1.9.0"),sQuery(id+"F4.wireOp",EDGE,"E7.3.9.0"),sQuery(id+"F4.wireOp",EDGE,"E8.3.10.0")])],"capPos":0.0});
            var Q4;
            Q4=makeQuery(id+"F12.opLoft","MID_CAP_EDGE",EDGE,{"disambiguationData":[OSD([sQuery(id+"F4.wireOp",EDGE,"E7.1.8.0"),sQuery(id+"F4.wireOp",EDGE,"E7.1.9.0"),sQuery(id+"F4.wireOp",EDGE,"E7.3.9.0")])],"capPos":0.0});
            var Q5;
            Q5=makeQuery(id+"F12.opLoft","MID_CAP_EDGE",EDGE,{"disambiguationData":[OSD([sQuery(id+"F4.wireOp",EDGE,"E6.1.0"),sQuery(id+"F4.wireOp",EDGE,"E6.1.1"),sQuery(id+"F4.wireOp",EDGE,"E6.2.1")])],"capPos":0.0});
            var Q6;
            Q6=makeQuery(id+"F12.opLoft","MID_CAP_EDGE",EDGE,{"disambiguationData":[OSD([sQuery(id+"F4.wireOp",EDGE,"E8.1.11.0"),sQuery(id+"F4.wireOp",EDGE,"E8.1.12.0"),sQuery(id+"F4.wireOp",EDGE,"E8.3.12.0")])],"capPos":2.0});
            var Q7;
            Q7=makeQuery(id+"F12.opLoft","MID_CAP_EDGE",EDGE,{"disambiguationData":[OSD([sQuery(id+"F4.wireOp",EDGE,"E6.1.0"),sQuery(id+"F4.wireOp",EDGE,"E6.2.0"),sQuery(id+"F4.wireOp",EDGE,"E6.2.1")])],"capPos":0.0});
            var Q8;
            Q8=makeQuery(id+"F12.opLoft","SWEPT_EDGE",EDGE,{"disambiguationData":[OSD([sQuery(id+"F4.wireOp",EDGE,"E8.1.11.0"),sQuery(id+"F4.wireOp",EDGE,"E8.3.11.0"),sQuery(id+"F4.wireOp",EDGE,"E8.1.12.0"),sQuery(id+"F4.wireOp",EDGE,"E8.3.12.0")])]});
            var Q9;
            Q9=makeQuery(id+"F12.opLoft","MID_CAP_EDGE",EDGE,{"disambiguationData":[OSD([sQuery(id+"F4.wireOp",EDGE,"E8.1.10.0"),sQuery(id+"F4.wireOp",EDGE,"E8.3.10.0"),sQuery(id+"F4.wireOp",EDGE,"E8.3.11.0")])],"capPos":2.0});
            var Q10;
            Q10=makeQuery(id+"F12.opLoft","SWEPT_EDGE",EDGE,{"disambiguationData":[OSD([sQuery(id+"F4.wireOp",EDGE,"E5"),sQuery(id+"F4.wireOp",EDGE,"E8.1.13.0"),sQuery(id+"F4.wireOp",EDGE,"E8.1.14.0"),sQuery(id+"F4.wireOp",EDGE,"E8.3.14.0")])]});
            var Q11;
            Q11=makeQuery(id+"F12.opLoft","SWEPT_EDGE",EDGE,{"disambiguationData":[OSD([sQuery(id+"F4.wireOp",EDGE,"E8.1.10.0"),sQuery(id+"F4.wireOp",EDGE,"E8.3.10.0"),sQuery(id+"F4.wireOp",EDGE,"E8.1.11.0"),sQuery(id+"F4.wireOp",EDGE,"E8.3.11.0")])]});
            var Q12;
            Q12=makeQuery(id+"F12.opLoft","MID_CAP_EDGE",EDGE,{"disambiguationData":[OSD([sQuery(id+"F4.wireOp",EDGE,"E8.1.12.0"),sQuery(id+"F4.wireOp",EDGE,"E8.3.12.0"),sQuery(id+"F4.wireOp",EDGE,"E8.3.13.0")])],"capPos":2.0});
            var Q13;
            Q13=makeQuery(id+"F12.opLoft","MID_CAP_EDGE",EDGE,{"disambiguationData":[OSD([sQuery(id+"F4.wireOp",EDGE,"E6.1.0"),sQuery(id+"F4.wireOp",EDGE,"E6.2.0"),sQuery(id+"F4.wireOp",EDGE,"E6.2.1")])],"capPos":2.0});
            var Q14;
            Q14=makeQuery(id+"F12.opLoft","MID_CAP_EDGE",EDGE,{"disambiguationData":[OSD([sQuery(id+"F4.wireOp",EDGE,"E6.6.0"),sQuery(id+"F4.wireOp",EDGE,"E6.7.0"),sQuery(id+"F4.wireOp",EDGE,"E6.7.1")])],"capPos":0.0});
            var Q15;
            Q15=makeQuery(id+"F12.opLoft","MID_CAP_EDGE",EDGE,{"disambiguationData":[OSD([sQuery(id+"F4.wireOp",EDGE,"E6.4.0"),sQuery(id+"F4.wireOp",EDGE,"E6.5.0"),sQuery(id+"F4.wireOp",EDGE,"E6.5.1")])],"capPos":0.0});
            var Q16;
            Q16=makeQuery(id+"F12.opLoft","SWEPT_EDGE",EDGE,{"disambiguationData":[OSD([sQuery(id+"F4.wireOp",EDGE,"E6.1.0"),sQuery(id+"F4.wireOp",EDGE,"E6.1.1"),sQuery(id+"F4.wireOp",EDGE,"E6.2.0"),sQuery(id+"F4.wireOp",EDGE,"E6.2.1")])]});
            var Q17;
            Q17=makeQuery(id+"F12.opLoft","SWEPT_EDGE",EDGE,{"disambiguationData":[OSD([sQuery(id+"F4.wireOp",EDGE,"E7.1.9.0"),sQuery(id+"F4.wireOp",EDGE,"E7.3.9.0"),sQuery(id+"F4.wireOp",EDGE,"E8.1.10.0"),sQuery(id+"F4.wireOp",EDGE,"E8.3.10.0")])]});
            var Q18;
            Q18=makeQuery(id+"F12.opLoft","MID_CAP_EDGE",EDGE,{"disambiguationData":[OSD([sQuery(id+"F4.wireOp",EDGE,"E4"),sQuery(id+"F4.wireOp",EDGE,"E5"),sQuery(id+"F4.wireOp",EDGE,"E8.1.14.0")])],"capPos":2.0});
            var Q19;
            Q19=makeQuery(id+"F12.opLoft","MID_CAP_EDGE",EDGE,{"disambiguationData":[OSD([sQuery(id+"F4.wireOp",EDGE,"E5"),sQuery(id+"F4.wireOp",EDGE,"E8.1.14.0"),sQuery(id+"F4.wireOp",EDGE,"E8.3.14.0")])],"capPos":0.0});
            var Q20;
            Q20=makeQuery(id+"F12.opLoft","SWEPT_EDGE",EDGE,{"disambiguationData":[OSD([sQuery(id+"F4.wireOp",EDGE,"E6.4.0"),sQuery(id+"F4.wireOp",EDGE,"E6.4.1"),sQuery(id+"F4.wireOp",EDGE,"E6.5.0"),sQuery(id+"F4.wireOp",EDGE,"E6.5.1")])]});
            var Q21;
            Q21=makeQuery(id+"F12.opLoft","SWEPT_EDGE",EDGE,{"disambiguationData":[OSD([sQuery(id+"F4.wireOp",EDGE,"E6.6.0"),sQuery(id+"F4.wireOp",EDGE,"E6.6.1"),sQuery(id+"F4.wireOp",EDGE,"E6.7.0"),sQuery(id+"F4.wireOp",EDGE,"E6.7.1")])]});
            var Q22;
            Q22=makeQuery(id+"F12.opLoft","SWEPT_EDGE",EDGE,{"disambiguationData":[OSD([sQuery(id+"F4.wireOp",EDGE,"E4"),sQuery(id+"F4.wireOp",EDGE,"E5"),sQuery(id+"F4.wireOp",EDGE,"E6.1.0"),sQuery(id+"F4.wireOp",EDGE,"E6.1.1")])]});
            var Q23;
            Q23=makeQuery(id+"F12.opLoft","SWEPT_EDGE",EDGE,{"disambiguationData":[OSD([sQuery(id+"F4.wireOp",EDGE,"E8.1.12.0"),sQuery(id+"F4.wireOp",EDGE,"E8.3.12.0"),sQuery(id+"F4.wireOp",EDGE,"E8.1.13.0"),sQuery(id+"F4.wireOp",EDGE,"E8.3.13.0")])]});
            var Q24;
            Q24=makeQuery(id+"F12.opLoft","MID_CAP_EDGE",EDGE,{"disambiguationData":[OSD([sQuery(id+"F4.wireOp",EDGE,"E8.1.13.0"),sQuery(id+"F4.wireOp",EDGE,"E8.3.13.0"),sQuery(id+"F4.wireOp",EDGE,"E8.3.14.0")])],"capPos":2.0});
            var Q25;
            Q25=makeQuery(id+"F12.opLoft","SWEPT_EDGE",EDGE,{"disambiguationData":[OSD([sQuery(id+"F4.wireOp",EDGE,"E8.1.11.0"),sQuery(id+"F4.wireOp",EDGE,"E8.1.12.0"),sQuery(id+"F4.wireOp",EDGE,"E8.3.12.0"),sQuery(id+"F4.wireOp",EDGE,"E8.3.13.0")])]});
            var Q26;
            Q26=makeQuery(id+"F12.opLoft","SWEPT_EDGE",EDGE,{"disambiguationData":[OSD([sQuery(id+"F4.wireOp",EDGE,"E8.1.12.0"),sQuery(id+"F4.wireOp",EDGE,"E8.1.13.0"),sQuery(id+"F4.wireOp",EDGE,"E8.3.13.0"),sQuery(id+"F4.wireOp",EDGE,"E8.3.14.0")])]});
            var Q27;
            Q27=makeQuery(id+"F12.opLoft","MID_CAP_EDGE",EDGE,{"disambiguationData":[OSD([sQuery(id+"F4.wireOp",EDGE,"E8.1.11.0"),sQuery(id+"F4.wireOp",EDGE,"E8.3.11.0"),sQuery(id+"F4.wireOp",EDGE,"E8.3.12.0")])],"capPos":0.0});
            var Q28;
            Q28=makeQuery(id+"F12.opLoft","MID_CAP_EDGE",EDGE,{"disambiguationData":[OSD([sQuery(id+"F4.wireOp",EDGE,"E8.1.13.0"),sQuery(id+"F4.wireOp",EDGE,"E8.3.13.0"),sQuery(id+"F4.wireOp",EDGE,"E8.3.14.0")])],"capPos":0.0});
            var Q29;
            Q29=makeQuery(id+"F12.opLoft","SWEPT_EDGE",EDGE,{"disambiguationData":[OSD([sQuery(id+"F4.wireOp",EDGE,"E8.1.13.0"),sQuery(id+"F4.wireOp",EDGE,"E8.3.13.0"),sQuery(id+"F4.wireOp",EDGE,"E8.1.14.0"),sQuery(id+"F4.wireOp",EDGE,"E8.3.14.0")])]});
            var Q30;
            Q30=makeQuery(id+"F12.opLoft","SWEPT_EDGE",EDGE,{"disambiguationData":[OSD([sQuery(id+"F4.wireOp",EDGE,"E6.7.0"),sQuery(id+"F4.wireOp",EDGE,"E6.7.1"),sQuery(id+"F4.wireOp",EDGE,"E7.1.8.0"),sQuery(id+"F4.wireOp",EDGE,"E7.3.8.0")])]});
            var Q31;
            Q31=makeQuery(id+"F12.opLoft","MID_CAP_EDGE",EDGE,{"disambiguationData":[OSD([sQuery(id+"F4.wireOp",EDGE,"E4"),sQuery(id+"F4.wireOp",EDGE,"E6.1.0"),sQuery(id+"F4.wireOp",EDGE,"E6.1.1")])],"capPos":0.0});
            var Q32;
            Q32=makeQuery(id+"F12.opLoft","MID_CAP_EDGE",EDGE,{"disambiguationData":[OSD([sQuery(id+"F4.wireOp",EDGE,"E8.1.12.0"),sQuery(id+"F4.wireOp",EDGE,"E8.1.13.0"),sQuery(id+"F4.wireOp",EDGE,"E8.3.13.0")])],"capPos":2.0});
            var Q33;
            Q33=makeQuery(id+"F12.opLoft","MID_CAP_EDGE",EDGE,{"disambiguationData":[OSD([sQuery(id+"F4.wireOp",EDGE,"E6.2.0"),sQuery(id+"F4.wireOp",EDGE,"E6.2.1"),sQuery(id+"F4.wireOp",EDGE,"E6.3.1")])],"capPos":0.0});
            var Q34;
            Q34=makeQuery(id+"F12.opLoft","SWEPT_EDGE",EDGE,{"disambiguationData":[OSD([sQuery(id+"F4.wireOp",EDGE,"E6.5.0"),sQuery(id+"F4.wireOp",EDGE,"E6.5.1"),sQuery(id+"F4.wireOp",EDGE,"E6.6.0"),sQuery(id+"F4.wireOp",EDGE,"E6.6.1")])]});
            var Q35;
            Q35=makeQuery(id+"F12.opLoft","MID_CAP_EDGE",EDGE,{"disambiguationData":[OSD([sQuery(id+"F4.wireOp",EDGE,"E8.1.13.0"),sQuery(id+"F4.wireOp",EDGE,"E8.1.14.0"),sQuery(id+"F4.wireOp",EDGE,"E8.3.14.0")])],"capPos":2.0});
            var Q36;
            Q36=makeQuery(id+"F12.opLoft","MID_CAP_EDGE",EDGE,{"disambiguationData":[OSD([sQuery(id+"F4.wireOp",EDGE,"E7.1.9.0"),sQuery(id+"F4.wireOp",EDGE,"E7.3.9.0"),sQuery(id+"F4.wireOp",EDGE,"E8.3.10.0")])],"capPos":2.0});
            var Q37;
            Q37=makeQuery(id+"F12.opLoft","MID_CAP_EDGE",EDGE,{"disambiguationData":[OSD([sQuery(id+"F4.wireOp",EDGE,"E6.3.0"),sQuery(id+"F4.wireOp",EDGE,"E6.4.0"),sQuery(id+"F4.wireOp",EDGE,"E6.4.1")])],"capPos":0.0});
            var Q38;
            Q38=makeQuery(id+"F12.opLoft","SWEPT_EDGE",EDGE,{"disambiguationData":[OSD([sQuery(id+"F4.wireOp",EDGE,"E7.1.9.0"),sQuery(id+"F4.wireOp",EDGE,"E8.1.10.0"),sQuery(id+"F4.wireOp",EDGE,"E8.3.10.0"),sQuery(id+"F4.wireOp",EDGE,"E8.3.11.0")])]});
            var Q39;
            Q39=makeQuery(id+"F12.opLoft","MID_CAP_EDGE",EDGE,{"disambiguationData":[OSD([sQuery(id+"F4.wireOp",EDGE,"E8.1.12.0"),sQuery(id+"F4.wireOp",EDGE,"E8.3.12.0"),sQuery(id+"F4.wireOp",EDGE,"E8.3.13.0")])],"capPos":0.0});
            var Q40;
            Q40=makeQuery(id+"F12.opLoft","MID_CAP_EDGE",EDGE,{"disambiguationData":[OSD([sQuery(id+"F4.wireOp",EDGE,"E6.3.0"),sQuery(id+"F4.wireOp",EDGE,"E6.3.1"),sQuery(id+"F4.wireOp",EDGE,"E6.4.1")])],"capPos":0.0});
            var Q41;
            Q41=makeQuery(id+"F12.opLoft","SWEPT_EDGE",EDGE,{"disambiguationData":[OSD([sQuery(id+"F4.wireOp",EDGE,"E7.1.8.0"),sQuery(id+"F4.wireOp",EDGE,"E7.3.8.0"),sQuery(id+"F4.wireOp",EDGE,"E7.1.9.0"),sQuery(id+"F4.wireOp",EDGE,"E7.3.9.0")])]});
            var Q42;
            Q42=makeQuery(id+"F12.opLoft","SWEPT_EDGE",EDGE,{"disambiguationData":[OSD([sQuery(id+"F4.wireOp",EDGE,"E8.1.10.0"),sQuery(id+"F4.wireOp",EDGE,"E8.1.11.0"),sQuery(id+"F4.wireOp",EDGE,"E8.3.11.0"),sQuery(id+"F4.wireOp",EDGE,"E8.3.12.0")])]});
            var Q43;
            Q43=makeQuery(id+"F12.opLoft","MID_CAP_EDGE",EDGE,{"disambiguationData":[OSD([sQuery(id+"F4.wireOp",EDGE,"E8.1.10.0"),sQuery(id+"F4.wireOp",EDGE,"E8.3.10.0"),sQuery(id+"F4.wireOp",EDGE,"E8.3.11.0")])],"capPos":0.0});
            var Q44;
            Q44=makeQuery(id+"F12.opLoft","MID_CAP_EDGE",EDGE,{"disambiguationData":[OSD([sQuery(id+"F4.wireOp",EDGE,"E8.1.12.0"),sQuery(id+"F4.wireOp",EDGE,"E8.1.13.0"),sQuery(id+"F4.wireOp",EDGE,"E8.3.13.0")])],"capPos":0.0});
            var Q45;
            Q45=makeQuery(id+"F12.opLoft","SWEPT_EDGE",EDGE,{"disambiguationData":[OSD([sQuery(id+"F4.wireOp",EDGE,"E6.7.0"),sQuery(id+"F4.wireOp",EDGE,"E7.1.8.0"),sQuery(id+"F4.wireOp",EDGE,"E7.3.8.0"),sQuery(id+"F4.wireOp",EDGE,"E7.3.9.0")])]});
            var Q46;
            Q46=makeQuery(id+"F12.opLoft","MID_CAP_EDGE",EDGE,{"disambiguationData":[OSD([sQuery(id+"F4.wireOp",EDGE,"E7.1.9.0"),sQuery(id+"F4.wireOp",EDGE,"E8.1.10.0"),sQuery(id+"F4.wireOp",EDGE,"E8.3.10.0")])],"capPos":0.0});
            var Q47;
            Q47=makeQuery(id+"F12.opLoft","MID_CAP_EDGE",EDGE,{"disambiguationData":[OSD([sQuery(id+"F4.wireOp",EDGE,"E6.5.0"),sQuery(id+"F4.wireOp",EDGE,"E6.5.1"),sQuery(id+"F4.wireOp",EDGE,"E6.6.1")])],"capPos":0.0});
            var Q48;
            Q48=makeQuery(id+"F12.opLoft","SWEPT_EDGE",EDGE,{"disambiguationData":[OSD([sQuery(id+"F4.wireOp",EDGE,"E4"),sQuery(id+"F4.wireOp",EDGE,"E5"),sQuery(id+"F4.wireOp",EDGE,"E8.1.14.0"),sQuery(id+"F4.wireOp",EDGE,"E8.3.14.0")])]});
            var Q49;
            Q49=makeQuery(id+"F12.opLoft","MID_CAP_EDGE",EDGE,{"disambiguationData":[OSD([sQuery(id+"F4.wireOp",EDGE,"E8.1.11.0"),sQuery(id+"F4.wireOp",EDGE,"E8.3.11.0"),sQuery(id+"F4.wireOp",EDGE,"E8.3.12.0")])],"capPos":2.0});
            var Q50;
            Q50=makeQuery(id+"F12.opLoft","MID_CAP_EDGE",EDGE,{"disambiguationData":[OSD([sQuery(id+"F4.wireOp",EDGE,"E6.1.0"),sQuery(id+"F4.wireOp",EDGE,"E6.1.1"),sQuery(id+"F4.wireOp",EDGE,"E6.2.1")])],"capPos":2.0});
            var Q51;
            Q51=makeQuery(id+"F12.opLoft","SWEPT_EDGE",EDGE,{"disambiguationData":[OSD([sQuery(id+"F4.wireOp",EDGE,"E6.6.0"),sQuery(id+"F4.wireOp",EDGE,"E6.7.0"),sQuery(id+"F4.wireOp",EDGE,"E6.7.1"),sQuery(id+"F4.wireOp",EDGE,"E7.3.8.0")])]});
            var Q52;
            Q52=makeQuery(id+"F12.opLoft","MID_CAP_EDGE",EDGE,{"disambiguationData":[OSD([sQuery(id+"F4.wireOp",EDGE,"E6.7.0"),sQuery(id+"F4.wireOp",EDGE,"E6.7.1"),sQuery(id+"F4.wireOp",EDGE,"E7.3.8.0")])],"capPos":0.0});
            var Q53;
            Q53=makeQuery(id+"F12.opLoft","SWEPT_EDGE",EDGE,{"disambiguationData":[OSD([sQuery(id+"F4.wireOp",EDGE,"E6.5.0"),sQuery(id+"F4.wireOp",EDGE,"E6.6.0"),sQuery(id+"F4.wireOp",EDGE,"E6.6.1"),sQuery(id+"F4.wireOp",EDGE,"E6.7.1")])]});
            var Q54;
            Q54=makeQuery(id+"F12.opLoft","MID_CAP_EDGE",EDGE,{"disambiguationData":[OSD([sQuery(id+"F4.wireOp",EDGE,"E4"),sQuery(id+"F4.wireOp",EDGE,"E5"),sQuery(id+"F4.wireOp",EDGE,"E6.1.1")])],"capPos":0.0});
            var Q55;
            Q55=makeQuery(id+"F12.opLoft","SWEPT_EDGE",EDGE,{"disambiguationData":[OSD([sQuery(id+"F4.wireOp",EDGE,"E6.3.0"),sQuery(id+"F4.wireOp",EDGE,"E6.4.0"),sQuery(id+"F4.wireOp",EDGE,"E6.4.1"),sQuery(id+"F4.wireOp",EDGE,"E6.5.1")])]});
            var Q56;
            Q56=makeQuery(id+"F12.opLoft","MID_CAP_EDGE",EDGE,{"disambiguationData":[OSD([sQuery(id+"F4.wireOp",EDGE,"E5"),sQuery(id+"F4.wireOp",EDGE,"E8.1.14.0"),sQuery(id+"F4.wireOp",EDGE,"E8.3.14.0")])],"capPos":2.0});
            var Q57;
            Q57=makeQuery(id+"F12.opLoft","MID_CAP_EDGE",EDGE,{"disambiguationData":[OSD([sQuery(id+"F4.wireOp",EDGE,"E4"),sQuery(id+"F4.wireOp",EDGE,"E5"),sQuery(id+"F4.wireOp",EDGE,"E6.1.1")])],"capPos":2.0});
            var Q58;
            Q58=makeQuery(id+"F12.opLoft","MID_CAP_EDGE",EDGE,{"disambiguationData":[OSD([sQuery(id+"F4.wireOp",EDGE,"E7.1.8.0"),sQuery(id+"F4.wireOp",EDGE,"E7.3.8.0"),sQuery(id+"F4.wireOp",EDGE,"E7.3.9.0")])],"capPos":2.0});
            var Q59;
            Q59=makeQuery(id+"F12.opLoft","MID_CAP_EDGE",EDGE,{"disambiguationData":[OSD([sQuery(id+"F4.wireOp",EDGE,"E6.7.0"),sQuery(id+"F4.wireOp",EDGE,"E6.7.1"),sQuery(id+"F4.wireOp",EDGE,"E7.3.8.0")])],"capPos":2.0});
            var Q60;
            Q60=makeQuery(id+"F12.opLoft","MID_CAP_EDGE",EDGE,{"disambiguationData":[OSD([sQuery(id+"F4.wireOp",EDGE,"E7.1.8.0"),sQuery(id+"F4.wireOp",EDGE,"E7.3.8.0"),sQuery(id+"F4.wireOp",EDGE,"E7.3.9.0")])],"capPos":0.0});
            var Q61;
            Q61=makeQuery(id+"F12.opLoft","MID_CAP_EDGE",EDGE,{"disambiguationData":[OSD([sQuery(id+"F4.wireOp",EDGE,"E6.2.0"),sQuery(id+"F4.wireOp",EDGE,"E6.2.1"),sQuery(id+"F4.wireOp",EDGE,"E6.3.1")])],"capPos":2.0});
            var Q62;
            Q62=makeQuery(id+"F12.opLoft","MID_CAP_EDGE",EDGE,{"disambiguationData":[OSD([sQuery(id+"F4.wireOp",EDGE,"E6.5.0"),sQuery(id+"F4.wireOp",EDGE,"E6.6.0"),sQuery(id+"F4.wireOp",EDGE,"E6.6.1")])],"capPos":0.0});
            var Q63;
            Q63=makeQuery(id+"F12.opLoft","SWEPT_EDGE",EDGE,{"disambiguationData":[OSD([sQuery(id+"F4.wireOp",EDGE,"E4"),sQuery(id+"F4.wireOp",EDGE,"E5"),sQuery(id+"F4.wireOp",EDGE,"E6.1.1"),sQuery(id+"F4.wireOp",EDGE,"E8.1.14.0")])]});
            var Q64;
            Q64=makeQuery(id+"F12.opLoft","MID_CAP_EDGE",EDGE,{"disambiguationData":[OSD([sQuery(id+"F4.wireOp",EDGE,"E6.5.0"),sQuery(id+"F4.wireOp",EDGE,"E6.5.1"),sQuery(id+"F4.wireOp",EDGE,"E6.6.1")])],"capPos":2.0});
            var Q65;
            Q65=makeQuery(id+"F12.opLoft","MID_CAP_EDGE",EDGE,{"disambiguationData":[OSD([sQuery(id+"F4.wireOp",EDGE,"E8.1.13.0"),sQuery(id+"F4.wireOp",EDGE,"E8.1.14.0"),sQuery(id+"F4.wireOp",EDGE,"E8.3.14.0")])],"capPos":0.0});
            var Q66;
            Q66=makeQuery(id+"F12.opLoft","MID_CAP_EDGE",EDGE,{"disambiguationData":[OSD([sQuery(id+"F4.wireOp",EDGE,"E6.7.0"),sQuery(id+"F4.wireOp",EDGE,"E7.1.8.0"),sQuery(id+"F4.wireOp",EDGE,"E7.3.8.0")])],"capPos":2.0});
            var Q67;
            Q67=makeQuery(id+"F12.opLoft","MID_CAP_EDGE",EDGE,{"disambiguationData":[OSD([sQuery(id+"F4.wireOp",EDGE,"E6.5.0"),sQuery(id+"F4.wireOp",EDGE,"E6.6.0"),sQuery(id+"F4.wireOp",EDGE,"E6.6.1")])],"capPos":2.0});
            var Q68;
            Q68=makeQuery(id+"F12.opLoft","MID_CAP_EDGE",EDGE,{"disambiguationData":[OSD([sQuery(id+"F4.wireOp",EDGE,"E8.1.11.0"),sQuery(id+"F4.wireOp",EDGE,"E8.1.12.0"),sQuery(id+"F4.wireOp",EDGE,"E8.3.12.0")])],"capPos":0.0});
            var Q69;
            Q69=makeQuery(id+"F12.opLoft","MID_CAP_EDGE",EDGE,{"disambiguationData":[OSD([sQuery(id+"F4.wireOp",EDGE,"E7.1.8.0"),sQuery(id+"F4.wireOp",EDGE,"E7.1.9.0"),sQuery(id+"F4.wireOp",EDGE,"E7.3.9.0")])],"capPos":2.0});
            var Q70;
            Q70=makeQuery(id+"F12.opLoft","SWEPT_EDGE",EDGE,{"disambiguationData":[OSD([sQuery(id+"F4.wireOp",EDGE,"E6.2.0"),sQuery(id+"F4.wireOp",EDGE,"E6.2.1"),sQuery(id+"F4.wireOp",EDGE,"E6.3.0"),sQuery(id+"F4.wireOp",EDGE,"E6.3.1")])]});
            var Q71;
            Q71=makeQuery(id+"F12.opLoft","SWEPT_EDGE",EDGE,{"disambiguationData":[OSD([sQuery(id+"F4.wireOp",EDGE,"E6.1.0"),sQuery(id+"F4.wireOp",EDGE,"E6.2.0"),sQuery(id+"F4.wireOp",EDGE,"E6.2.1"),sQuery(id+"F4.wireOp",EDGE,"E6.3.1")])]});
            var Q72;
            Q72=makeQuery(id+"F12.opLoft","MID_CAP_EDGE",EDGE,{"disambiguationData":[OSD([sQuery(id+"F4.wireOp",EDGE,"E4"),sQuery(id+"F4.wireOp",EDGE,"E6.1.0"),sQuery(id+"F4.wireOp",EDGE,"E6.1.1")])],"capPos":2.0});
            var Q73;
            Q73=makeQuery(id+"F12.opLoft","MID_CAP_EDGE",EDGE,{"disambiguationData":[OSD([sQuery(id+"F4.wireOp",EDGE,"E7.1.9.0"),sQuery(id+"F4.wireOp",EDGE,"E8.1.10.0"),sQuery(id+"F4.wireOp",EDGE,"E8.3.10.0")])],"capPos":2.0});
            var Q74;
            Q74=makeQuery(id+"F12.opLoft","SWEPT_EDGE",EDGE,{"disambiguationData":[OSD([sQuery(id+"F4.wireOp",EDGE,"E4"),sQuery(id+"F4.wireOp",EDGE,"E6.1.0"),sQuery(id+"F4.wireOp",EDGE,"E6.1.1"),sQuery(id+"F4.wireOp",EDGE,"E6.2.1")])]});
            var Q75;
            Q75=makeQuery(id+"F12.opLoft","MID_CAP_EDGE",EDGE,{"disambiguationData":[OSD([sQuery(id+"F4.wireOp",EDGE,"E6.4.0"),sQuery(id+"F4.wireOp",EDGE,"E6.4.1"),sQuery(id+"F4.wireOp",EDGE,"E6.5.1")])],"capPos":2.0});
            var Q76;
            Q76=makeQuery(id+"F12.opLoft","MID_CAP_EDGE",EDGE,{"disambiguationData":[OSD([sQuery(id+"F4.wireOp",EDGE,"E6.4.0"),sQuery(id+"F4.wireOp",EDGE,"E6.4.1"),sQuery(id+"F4.wireOp",EDGE,"E6.5.1")])],"capPos":0.0});
            var Q77;
            Q77=makeQuery(id+"F12.opLoft","MID_CAP_EDGE",EDGE,{"disambiguationData":[OSD([sQuery(id+"F4.wireOp",EDGE,"E6.4.0"),sQuery(id+"F4.wireOp",EDGE,"E6.5.0"),sQuery(id+"F4.wireOp",EDGE,"E6.5.1")])],"capPos":2.0});
            var Q78;
            Q78=makeQuery(id+"F12.opLoft","SWEPT_EDGE",EDGE,{"disambiguationData":[OSD([sQuery(id+"F4.wireOp",EDGE,"E6.4.0"),sQuery(id+"F4.wireOp",EDGE,"E6.5.0"),sQuery(id+"F4.wireOp",EDGE,"E6.5.1"),sQuery(id+"F4.wireOp",EDGE,"E6.6.1")])]});
            var Q79;
            Q79=makeQuery(id+"F12.opLoft","MID_CAP_EDGE",EDGE,{"disambiguationData":[OSD([sQuery(id+"F4.wireOp",EDGE,"E6.6.0"),sQuery(id+"F4.wireOp",EDGE,"E6.6.1"),sQuery(id+"F4.wireOp",EDGE,"E6.7.1")])],"capPos":0.0});
            var Q80;
            Q80=makeQuery(id+"F12.opLoft","MID_CAP_EDGE",EDGE,{"disambiguationData":[OSD([sQuery(id+"F4.wireOp",EDGE,"E6.2.0"),sQuery(id+"F4.wireOp",EDGE,"E6.3.0"),sQuery(id+"F4.wireOp",EDGE,"E6.3.1")])],"capPos":0.0});
            var Q81;
            Q81=makeQuery(id+"F12.opLoft","MID_CAP_EDGE",EDGE,{"disambiguationData":[OSD([sQuery(id+"F4.wireOp",EDGE,"E8.1.10.0"),sQuery(id+"F4.wireOp",EDGE,"E8.1.11.0"),sQuery(id+"F4.wireOp",EDGE,"E8.3.11.0")])],"capPos":0.0});
            var Q82;
            Q82=makeQuery(id+"F12.opLoft","MID_CAP_EDGE",EDGE,{"disambiguationData":[OSD([sQuery(id+"F4.wireOp",EDGE,"E8.1.10.0"),sQuery(id+"F4.wireOp",EDGE,"E8.1.11.0"),sQuery(id+"F4.wireOp",EDGE,"E8.3.11.0")])],"capPos":2.0});
            var Q83;
            Q83=makeQuery(id+"F12.opLoft","SWEPT_EDGE",EDGE,{"disambiguationData":[OSD([sQuery(id+"F4.wireOp",EDGE,"E6.3.0"),sQuery(id+"F4.wireOp",EDGE,"E6.3.1"),sQuery(id+"F4.wireOp",EDGE,"E6.4.0"),sQuery(id+"F4.wireOp",EDGE,"E6.4.1")])]});
            var Q84;
            Q84=makeQuery(id+"F12.opLoft","MID_CAP_EDGE",EDGE,{"disambiguationData":[OSD([sQuery(id+"F4.wireOp",EDGE,"E6.3.0"),sQuery(id+"F4.wireOp",EDGE,"E6.3.1"),sQuery(id+"F4.wireOp",EDGE,"E6.4.1")])],"capPos":2.0});
            var Q85;
            Q85=makeQuery(id+"F12.opLoft","MID_CAP_EDGE",EDGE,{"disambiguationData":[OSD([sQuery(id+"F4.wireOp",EDGE,"E6.3.0"),sQuery(id+"F4.wireOp",EDGE,"E6.4.0"),sQuery(id+"F4.wireOp",EDGE,"E6.4.1")])],"capPos":2.0});
            var Q86;
            Q86=makeQuery(id+"F12.opLoft","MID_CAP_EDGE",EDGE,{"disambiguationData":[OSD([sQuery(id+"F4.wireOp",EDGE,"E6.7.0"),sQuery(id+"F4.wireOp",EDGE,"E7.1.8.0"),sQuery(id+"F4.wireOp",EDGE,"E7.3.8.0")])],"capPos":0.0});
            var Q87;
            Q87=makeQuery(id+"F12.opLoft","MID_CAP_EDGE",EDGE,{"disambiguationData":[OSD([sQuery(id+"F4.wireOp",EDGE,"E6.6.0"),sQuery(id+"F4.wireOp",EDGE,"E6.7.0"),sQuery(id+"F4.wireOp",EDGE,"E6.7.1")])],"capPos":2.0});
            var Q88;
            Q88=makeQuery(id+"F12.opLoft","MID_CAP_EDGE",EDGE,{"disambiguationData":[OSD([sQuery(id+"F4.wireOp",EDGE,"E6.2.0"),sQuery(id+"F4.wireOp",EDGE,"E6.3.0"),sQuery(id+"F4.wireOp",EDGE,"E6.3.1")])],"capPos":2.0});
            var Q89;
            Q89=makeQuery(id+"F12.opLoft","SWEPT_EDGE",EDGE,{"disambiguationData":[OSD([sQuery(id+"F4.wireOp",EDGE,"E6.2.0"),sQuery(id+"F4.wireOp",EDGE,"E6.3.0"),sQuery(id+"F4.wireOp",EDGE,"E6.3.1"),sQuery(id+"F4.wireOp",EDGE,"E6.4.1")])]});
            var Q90;
            Q90=makeQuery(id+"F12.opLoft","MID_CAP_EDGE",EDGE,{"disambiguationData":[OSD([sQuery(id+"F4.wireOp",EDGE,"E4"),sQuery(id+"F4.wireOp",EDGE,"E5"),sQuery(id+"F4.wireOp",EDGE,"E8.1.14.0")])],"capPos":0.0});
            var Q91;
            Q91=makeQuery(id+"F12.opLoft","MID_CAP_EDGE",EDGE,{"disambiguationData":[OSD([sQuery(id+"F4.wireOp",EDGE,"E6.6.0"),sQuery(id+"F4.wireOp",EDGE,"E6.6.1"),sQuery(id+"F4.wireOp",EDGE,"E6.7.1")])],"capPos":2.0});
            fillet(context, id + "F13", {"entities" : qUnion([Q0, Q1, Q2, Q3, Q4, Q5, Q6, Q7, Q8, Q9, Q10, Q11, Q12, Q13, Q14, Q15, Q16, Q17, Q18, Q19, Q20, Q21, Q22, Q23, Q24, Q25, Q26, Q27, Q28, Q29, Q30, Q31, Q32, Q33, Q34, Q35, Q36, Q37, Q38, Q39, Q40, Q41, Q42, Q43, Q44, Q45, Q46, Q47, Q48, Q49, Q50, Q51, Q52, Q53, Q54, Q55, Q56, Q57, Q58, Q59, Q60, Q61, Q62, Q63, Q64, Q65, Q66, Q67, Q68, Q69, Q70, Q71, Q72, Q73, Q74, Q75, Q76, Q77, Q78, Q79, Q80, Q81, Q82, Q83, Q84, Q85, Q86, Q87, Q88, Q89, Q90, Q91]), "radius" : 1.25 * mm, "tangentPropagation" : true, "allowEdgeOverflow" : false});
        }
    });
